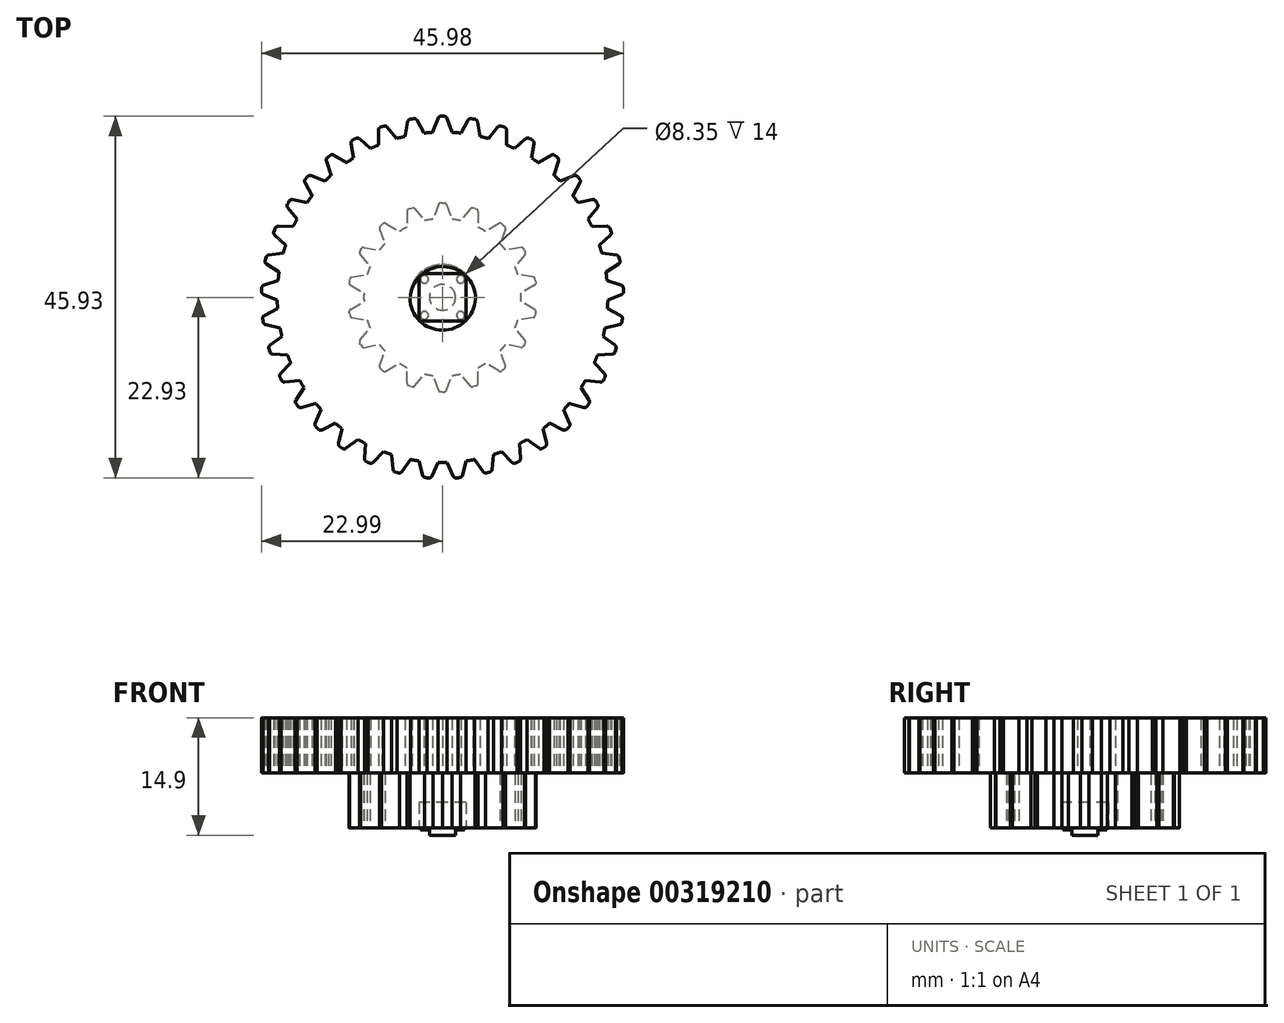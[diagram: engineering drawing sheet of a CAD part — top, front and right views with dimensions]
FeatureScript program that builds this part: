
annotation { "Feature Type Name" : "Feature", "Feature Type Description" : "" }
export const myFeature = defineFeature(function(context is Context, id is Id, definition is map)
    precondition{}
    {
        {
            var Q0;
            Q0=qCreatedBy(makeId("Top.planeOp"),FACE);
            var sketch = newSketch(context, id + "F0", { "sketchPlane" : qUnion([Q0])});
            skCircle(sketch, "E0", {"center": v(0, 0) * mm, "radius": 11 * mm, "construction": true});
            skCircle(sketch, "E1", {"center": v(0, 0) * mm, "radius": 10 * mm});
            skCircle(sketch, "E2", {"center": v(0, 0) * mm, "radius": 12 * mm, "construction": true});
            skPoint(sketch, "E3", {"position": v(10, 0) * mm});
            skPoint(sketch, "E4", {"position": v(11, 0) * mm});
            skPoint(sketch, "E5", {"position": v(12, 0) * mm});
            skLineSegment(sketch, "E6", {"start": v(-0.52, 11.8) * mm, "end": v(-1.2, 9.93) * mm});
            skLineSegment(sketch, "E7", {"start": v(0, 9.19) * mm, "end": v(0, 12) * mm});
            skLineSegment(sketch, "E8", {"start": v(0, 12) * mm, "end": v(-0.24, 12) * mm});
            skPoint(sketch, "E9.visualSharp", {"position": v(-0.45, 12) * mm});
            skArc(sketch, "E9.filletArc", {"start": v(-0.24, 12) * mm, "mid": v(-0.41, 11.94) * mm, "end": v(-0.52, 11.8) * mm});
            skLineSegment(sketch, "E10.MirrorCS", {"start": v(0, 12) * mm, "end": v(0.24, 12) * mm});
            skArc(sketch, "E11.MirrorCS", {"start": v(0.24, 12) * mm, "mid": v(0.41, 11.94) * mm, "end": v(0.52, 11.8) * mm});
            skLineSegment(sketch, "E12.MirrorCS", {"start": v(0.52, 11.8) * mm, "end": v(1.2, 9.93) * mm});
            skLineSegment(sketch, "E13.1.0", {"start": v(-3.55, 11.26) * mm, "end": v(-2.27, 9.74) * mm});
            skLineSegment(sketch, "E13.1.1", {"start": v(-4.52, 10.9) * mm, "end": v(-4.52, 8.92) * mm});
            skArc(sketch, "E13.1.2", {"start": v(-3.87, 11.36) * mm, "mid": v(-3.7, 11.36) * mm, "end": v(-3.55, 11.26) * mm});
            skArc(sketch, "E13.1.3", {"start": v(-4.33, 11.19) * mm, "mid": v(-4.47, 11.08) * mm, "end": v(-4.52, 10.9) * mm});
            skLineSegment(sketch, "E13.1.4", {"start": v(-4.1, 11.28) * mm, "end": v(-3.87, 11.36) * mm});
            skLineSegment(sketch, "E13.1.5", {"start": v(-4.1, 11.28) * mm, "end": v(-4.33, 11.19) * mm});
            skLineSegment(sketch, "E13.2.0", {"start": v(-7.19, 9.37) * mm, "end": v(-5.46, 8.38) * mm});
            skLineSegment(sketch, "E13.2.1", {"start": v(-7.98, 8.7) * mm, "end": v(-7.3, 6.83) * mm});
            skArc(sketch, "E13.2.2", {"start": v(-7.52, 9.35) * mm, "mid": v(-7.36, 9.41) * mm, "end": v(-7.19, 9.37) * mm});
            skArc(sketch, "E13.2.3", {"start": v(-7.9, 9.03) * mm, "mid": v(-8, 8.88) * mm, "end": v(-7.98, 8.7) * mm});
            skLineSegment(sketch, "E13.2.4", {"start": v(-7.71, 9.2) * mm, "end": v(-7.52, 9.35) * mm});
            skLineSegment(sketch, "E13.2.5", {"start": v(-7.71, 9.2) * mm, "end": v(-7.9, 9.03) * mm});
            skLineSegment(sketch, "E13.3.0", {"start": v(-9.96, 6.35) * mm, "end": v(-8, 6) * mm});
            skLineSegment(sketch, "E13.3.1", {"start": v(-10.48, 5.45) * mm, "end": v(-9.2, 3.92) * mm});
            skArc(sketch, "E13.3.2", {"start": v(-10.27, 6.2) * mm, "mid": v(-10.13, 6.33) * mm, "end": v(-9.96, 6.35) * mm});
            skArc(sketch, "E13.3.3", {"start": v(-10.51, 5.79) * mm, "mid": v(-10.55, 5.61) * mm, "end": v(-10.48, 5.45) * mm});
            skLineSegment(sketch, "E13.3.4", {"start": v(-10.4, 6) * mm, "end": v(-10.27, 6.2) * mm});
            skLineSegment(sketch, "E13.3.5", {"start": v(-10.4, 6) * mm, "end": v(-10.51, 5.79) * mm});
            skLineSegment(sketch, "E13.4.0", {"start": v(-11.53, 2.56) * mm, "end": v(-9.57, 2.9) * mm});
            skLineSegment(sketch, "E13.4.1", {"start": v(-11.7, 1.54) * mm, "end": v(-9.99, 0.54) * mm});
            skArc(sketch, "E13.4.2", {"start": v(-11.77, 2.32) * mm, "mid": v(-11.69, 2.48) * mm, "end": v(-11.53, 2.56) * mm});
            skArc(sketch, "E13.4.3", {"start": v(-11.86, 1.84) * mm, "mid": v(-11.83, 1.67) * mm, "end": v(-11.7, 1.54) * mm});
            skLineSegment(sketch, "E13.4.4", {"start": v(-11.82, 2.08) * mm, "end": v(-11.77, 2.32) * mm});
            skLineSegment(sketch, "E13.4.5", {"start": v(-11.82, 2.08) * mm, "end": v(-11.86, 1.84) * mm});
            skLineSegment(sketch, "E13.5.0", {"start": v(-11.7, -1.54) * mm, "end": v(-9.99, -0.54) * mm});
            skLineSegment(sketch, "E13.5.1", {"start": v(-11.53, -2.56) * mm, "end": v(-9.57, -2.9) * mm});
            skArc(sketch, "E13.5.2", {"start": v(-11.86, -1.84) * mm, "mid": v(-11.83, -1.67) * mm, "end": v(-11.7, -1.54) * mm});
            skArc(sketch, "E13.5.3", {"start": v(-11.77, -2.32) * mm, "mid": v(-11.69, -2.48) * mm, "end": v(-11.53, -2.56) * mm});
            skLineSegment(sketch, "E13.5.4", {"start": v(-11.82, -2.08) * mm, "end": v(-11.86, -1.84) * mm});
            skLineSegment(sketch, "E13.5.5", {"start": v(-11.82, -2.08) * mm, "end": v(-11.77, -2.32) * mm});
            skLineSegment(sketch, "E13.6.0", {"start": v(-10.48, -5.45) * mm, "end": v(-9.2, -3.92) * mm});
            skLineSegment(sketch, "E13.6.1", {"start": v(-9.96, -6.35) * mm, "end": v(-8, -6) * mm});
            skArc(sketch, "E13.6.2", {"start": v(-10.51, -5.79) * mm, "mid": v(-10.55, -5.61) * mm, "end": v(-10.48, -5.45) * mm});
            skArc(sketch, "E13.6.3", {"start": v(-10.27, -6.2) * mm, "mid": v(-10.13, -6.33) * mm, "end": v(-9.96, -6.35) * mm});
            skLineSegment(sketch, "E13.6.4", {"start": v(-10.4, -6) * mm, "end": v(-10.51, -5.79) * mm});
            skLineSegment(sketch, "E13.6.5", {"start": v(-10.4, -6) * mm, "end": v(-10.27, -6.2) * mm});
            skLineSegment(sketch, "E13.7.0", {"start": v(-7.98, -8.7) * mm, "end": v(-7.3, -6.83) * mm});
            skLineSegment(sketch, "E13.7.1", {"start": v(-7.19, -9.37) * mm, "end": v(-5.46, -8.38) * mm});
            skArc(sketch, "E13.7.2", {"start": v(-7.9, -9.03) * mm, "mid": v(-8, -8.88) * mm, "end": v(-7.98, -8.7) * mm});
            skArc(sketch, "E13.7.3", {"start": v(-7.52, -9.35) * mm, "mid": v(-7.36, -9.41) * mm, "end": v(-7.19, -9.37) * mm});
            skLineSegment(sketch, "E13.7.4", {"start": v(-7.71, -9.2) * mm, "end": v(-7.9, -9.03) * mm});
            skLineSegment(sketch, "E13.7.5", {"start": v(-7.71, -9.2) * mm, "end": v(-7.52, -9.35) * mm});
            skLineSegment(sketch, "E13.8.0", {"start": v(-4.52, -10.9) * mm, "end": v(-4.52, -8.92) * mm});
            skLineSegment(sketch, "E13.8.1", {"start": v(-3.55, -11.26) * mm, "end": v(-2.27, -9.74) * mm});
            skArc(sketch, "E13.8.2", {"start": v(-4.33, -11.19) * mm, "mid": v(-4.47, -11.08) * mm, "end": v(-4.52, -10.9) * mm});
            skArc(sketch, "E13.8.3", {"start": v(-3.87, -11.36) * mm, "mid": v(-3.7, -11.36) * mm, "end": v(-3.55, -11.26) * mm});
            skLineSegment(sketch, "E13.8.4", {"start": v(-4.1, -11.28) * mm, "end": v(-4.33, -11.19) * mm});
            skLineSegment(sketch, "E13.8.5", {"start": v(-4.1, -11.28) * mm, "end": v(-3.87, -11.36) * mm});
            skLineSegment(sketch, "E13.9.0", {"start": v(-0.52, -11.8) * mm, "end": v(-1.2, -9.93) * mm});
            skLineSegment(sketch, "E13.9.1", {"start": v(0.52, -11.8) * mm, "end": v(1.2, -9.93) * mm});
            skArc(sketch, "E13.9.2", {"start": v(-0.24, -12) * mm, "mid": v(-0.41, -11.94) * mm, "end": v(-0.52, -11.8) * mm});
            skArc(sketch, "E13.9.3", {"start": v(0.24, -12) * mm, "mid": v(0.41, -11.94) * mm, "end": v(0.52, -11.8) * mm});
            skLineSegment(sketch, "E13.9.4", {"start": v(0, -12) * mm, "end": v(-0.24, -12) * mm});
            skLineSegment(sketch, "E13.9.5", {"start": v(0, -12) * mm, "end": v(0.24, -12) * mm});
            skLineSegment(sketch, "E13.10.0", {"start": v(3.55, -11.26) * mm, "end": v(2.27, -9.74) * mm});
            skLineSegment(sketch, "E13.10.1", {"start": v(4.52, -10.9) * mm, "end": v(4.52, -8.92) * mm});
            skArc(sketch, "E13.10.2", {"start": v(3.87, -11.36) * mm, "mid": v(3.7, -11.36) * mm, "end": v(3.55, -11.26) * mm});
            skArc(sketch, "E13.10.3", {"start": v(4.33, -11.19) * mm, "mid": v(4.47, -11.08) * mm, "end": v(4.52, -10.9) * mm});
            skLineSegment(sketch, "E13.10.4", {"start": v(4.1, -11.28) * mm, "end": v(3.87, -11.36) * mm});
            skLineSegment(sketch, "E13.10.5", {"start": v(4.1, -11.28) * mm, "end": v(4.33, -11.19) * mm});
            skLineSegment(sketch, "E13.11.0", {"start": v(7.19, -9.37) * mm, "end": v(5.46, -8.38) * mm});
            skLineSegment(sketch, "E13.11.1", {"start": v(7.98, -8.7) * mm, "end": v(7.3, -6.83) * mm});
            skArc(sketch, "E13.11.2", {"start": v(7.52, -9.35) * mm, "mid": v(7.36, -9.41) * mm, "end": v(7.19, -9.37) * mm});
            skArc(sketch, "E13.11.3", {"start": v(7.9, -9.03) * mm, "mid": v(8, -8.88) * mm, "end": v(7.98, -8.7) * mm});
            skLineSegment(sketch, "E13.11.4", {"start": v(7.71, -9.2) * mm, "end": v(7.52, -9.35) * mm});
            skLineSegment(sketch, "E13.11.5", {"start": v(7.71, -9.2) * mm, "end": v(7.9, -9.03) * mm});
            skLineSegment(sketch, "E13.12.0", {"start": v(9.96, -6.35) * mm, "end": v(8, -6) * mm});
            skLineSegment(sketch, "E13.12.1", {"start": v(10.48, -5.45) * mm, "end": v(9.2, -3.92) * mm});
            skArc(sketch, "E13.12.2", {"start": v(10.27, -6.2) * mm, "mid": v(10.13, -6.33) * mm, "end": v(9.96, -6.35) * mm});
            skArc(sketch, "E13.12.3", {"start": v(10.51, -5.79) * mm, "mid": v(10.55, -5.61) * mm, "end": v(10.48, -5.45) * mm});
            skLineSegment(sketch, "E13.12.4", {"start": v(10.4, -6) * mm, "end": v(10.27, -6.2) * mm});
            skLineSegment(sketch, "E13.12.5", {"start": v(10.4, -6) * mm, "end": v(10.51, -5.79) * mm});
            skLineSegment(sketch, "E13.13.0", {"start": v(11.53, -2.56) * mm, "end": v(9.57, -2.9) * mm});
            skLineSegment(sketch, "E13.13.1", {"start": v(11.7, -1.54) * mm, "end": v(9.99, -0.54) * mm});
            skArc(sketch, "E13.13.2", {"start": v(11.77, -2.32) * mm, "mid": v(11.69, -2.48) * mm, "end": v(11.53, -2.56) * mm});
            skArc(sketch, "E13.13.3", {"start": v(11.86, -1.84) * mm, "mid": v(11.83, -1.67) * mm, "end": v(11.7, -1.54) * mm});
            skLineSegment(sketch, "E13.13.4", {"start": v(11.82, -2.08) * mm, "end": v(11.77, -2.32) * mm});
            skLineSegment(sketch, "E13.13.5", {"start": v(11.82, -2.08) * mm, "end": v(11.86, -1.84) * mm});
            skLineSegment(sketch, "E13.14.0", {"start": v(11.7, 1.54) * mm, "end": v(9.99, 0.54) * mm});
            skLineSegment(sketch, "E13.14.1", {"start": v(11.53, 2.56) * mm, "end": v(9.57, 2.9) * mm});
            skArc(sketch, "E13.14.2", {"start": v(11.86, 1.84) * mm, "mid": v(11.83, 1.67) * mm, "end": v(11.7, 1.54) * mm});
            skArc(sketch, "E13.14.3", {"start": v(11.77, 2.32) * mm, "mid": v(11.69, 2.48) * mm, "end": v(11.53, 2.56) * mm});
            skLineSegment(sketch, "E13.14.4", {"start": v(11.82, 2.08) * mm, "end": v(11.86, 1.84) * mm});
            skLineSegment(sketch, "E13.14.5", {"start": v(11.82, 2.08) * mm, "end": v(11.77, 2.32) * mm});
            skLineSegment(sketch, "E13.15.0", {"start": v(10.48, 5.45) * mm, "end": v(9.2, 3.92) * mm});
            skLineSegment(sketch, "E13.15.1", {"start": v(9.96, 6.35) * mm, "end": v(8, 6) * mm});
            skArc(sketch, "E13.15.2", {"start": v(10.51, 5.79) * mm, "mid": v(10.55, 5.61) * mm, "end": v(10.48, 5.45) * mm});
            skArc(sketch, "E13.15.3", {"start": v(10.27, 6.2) * mm, "mid": v(10.13, 6.33) * mm, "end": v(9.96, 6.35) * mm});
            skLineSegment(sketch, "E13.15.4", {"start": v(10.4, 6) * mm, "end": v(10.51, 5.79) * mm});
            skLineSegment(sketch, "E13.15.5", {"start": v(10.4, 6) * mm, "end": v(10.27, 6.2) * mm});
            skLineSegment(sketch, "E13.16.0", {"start": v(7.98, 8.7) * mm, "end": v(7.3, 6.83) * mm});
            skLineSegment(sketch, "E13.16.1", {"start": v(7.19, 9.37) * mm, "end": v(5.46, 8.38) * mm});
            skArc(sketch, "E13.16.2", {"start": v(7.9, 9.03) * mm, "mid": v(8, 8.88) * mm, "end": v(7.98, 8.7) * mm});
            skArc(sketch, "E13.16.3", {"start": v(7.52, 9.35) * mm, "mid": v(7.36, 9.41) * mm, "end": v(7.19, 9.37) * mm});
            skLineSegment(sketch, "E13.16.4", {"start": v(7.71, 9.2) * mm, "end": v(7.9, 9.03) * mm});
            skLineSegment(sketch, "E13.16.5", {"start": v(7.71, 9.2) * mm, "end": v(7.52, 9.35) * mm});
            skLineSegment(sketch, "E13.17.0", {"start": v(4.52, 10.9) * mm, "end": v(4.52, 8.92) * mm});
            skLineSegment(sketch, "E13.17.1", {"start": v(3.55, 11.26) * mm, "end": v(2.27, 9.74) * mm});
            skArc(sketch, "E13.17.2", {"start": v(4.33, 11.19) * mm, "mid": v(4.47, 11.08) * mm, "end": v(4.52, 10.9) * mm});
            skArc(sketch, "E13.17.3", {"start": v(3.87, 11.36) * mm, "mid": v(3.7, 11.36) * mm, "end": v(3.55, 11.26) * mm});
            skLineSegment(sketch, "E13.17.4", {"start": v(4.1, 11.28) * mm, "end": v(4.33, 11.19) * mm});
            skLineSegment(sketch, "E13.17.5", {"start": v(4.1, 11.28) * mm, "end": v(3.87, 11.36) * mm});
            skCircle(sketch, "E14", {"center": v(0, 0) * mm, "radius": 4.17 * mm});
            skSolve(sketch);
        }
        {
            var Q0;
            Q0 = qSketchRegion(id + "F0", true);
            extrude(context, id + "F1", {"entities" : qUnion([Q0]), "depth" : 7 * mm});
        }
        {
            var Q0;
            Q0=makeQuery(id+"F1.opExtrude","CAP_FACE",FACE,{"disambiguationData":[OSD([sQuery(id+"F0.wireOp",EDGE,"E1"),sQuery(id+"F0.wireOp",EDGE,"E6"),sQuery(id+"F0.wireOp",EDGE,"E8"),sQuery(id+"F0.wireOp",EDGE,"E9.filletArc"),sQuery(id+"F0.wireOp",EDGE,"E10.MirrorCS"),sQuery(id+"F0.wireOp",EDGE,"E11.MirrorCS"),sQuery(id+"F0.wireOp",EDGE,"E12.MirrorCS"),sQuery(id+"F0.wireOp",EDGE,"E13.1.0"),sQuery(id+"F0.wireOp",EDGE,"E13.1.1"),sQuery(id+"F0.wireOp",EDGE,"E13.1.2"),sQuery(id+"F0.wireOp",EDGE,"E13.1.3"),sQuery(id+"F0.wireOp",EDGE,"E13.1.4"),sQuery(id+"F0.wireOp",EDGE,"E13.1.5"),sQuery(id+"F0.wireOp",EDGE,"E13.2.0"),sQuery(id+"F0.wireOp",EDGE,"E13.2.1"),sQuery(id+"F0.wireOp",EDGE,"E13.2.2"),sQuery(id+"F0.wireOp",EDGE,"E13.2.3"),sQuery(id+"F0.wireOp",EDGE,"E13.2.4"),sQuery(id+"F0.wireOp",EDGE,"E13.2.5"),sQuery(id+"F0.wireOp",EDGE,"E13.3.0"),sQuery(id+"F0.wireOp",EDGE,"E13.3.1"),sQuery(id+"F0.wireOp",EDGE,"E13.3.2"),sQuery(id+"F0.wireOp",EDGE,"E13.3.3"),sQuery(id+"F0.wireOp",EDGE,"E13.3.4"),sQuery(id+"F0.wireOp",EDGE,"E13.3.5"),sQuery(id+"F0.wireOp",EDGE,"E13.4.0"),sQuery(id+"F0.wireOp",EDGE,"E13.4.1"),sQuery(id+"F0.wireOp",EDGE,"E13.4.2"),sQuery(id+"F0.wireOp",EDGE,"E13.4.3"),sQuery(id+"F0.wireOp",EDGE,"E13.4.4"),sQuery(id+"F0.wireOp",EDGE,"E13.4.5"),sQuery(id+"F0.wireOp",EDGE,"E13.5.0"),sQuery(id+"F0.wireOp",EDGE,"E13.5.1"),sQuery(id+"F0.wireOp",EDGE,"E13.5.2"),sQuery(id+"F0.wireOp",EDGE,"E13.5.3"),sQuery(id+"F0.wireOp",EDGE,"E13.5.4"),sQuery(id+"F0.wireOp",EDGE,"E13.5.5"),sQuery(id+"F0.wireOp",EDGE,"E13.6.0"),sQuery(id+"F0.wireOp",EDGE,"E13.6.1"),sQuery(id+"F0.wireOp",EDGE,"E13.6.2"),sQuery(id+"F0.wireOp",EDGE,"E13.6.3"),sQuery(id+"F0.wireOp",EDGE,"E13.6.4"),sQuery(id+"F0.wireOp",EDGE,"E13.6.5"),sQuery(id+"F0.wireOp",EDGE,"E13.7.0"),sQuery(id+"F0.wireOp",EDGE,"E13.7.1"),sQuery(id+"F0.wireOp",EDGE,"E13.7.2"),sQuery(id+"F0.wireOp",EDGE,"E13.7.3"),sQuery(id+"F0.wireOp",EDGE,"E13.7.4"),sQuery(id+"F0.wireOp",EDGE,"E13.7.5"),sQuery(id+"F0.wireOp",EDGE,"E13.8.0"),sQuery(id+"F0.wireOp",EDGE,"E13.8.1"),sQuery(id+"F0.wireOp",EDGE,"E13.8.2"),sQuery(id+"F0.wireOp",EDGE,"E13.8.3"),sQuery(id+"F0.wireOp",EDGE,"E13.8.4"),sQuery(id+"F0.wireOp",EDGE,"E13.8.5"),sQuery(id+"F0.wireOp",EDGE,"E13.9.0"),sQuery(id+"F0.wireOp",EDGE,"E13.9.1"),sQuery(id+"F0.wireOp",EDGE,"E13.9.2"),sQuery(id+"F0.wireOp",EDGE,"E13.9.3"),sQuery(id+"F0.wireOp",EDGE,"E13.9.4"),sQuery(id+"F0.wireOp",EDGE,"E13.9.5"),sQuery(id+"F0.wireOp",EDGE,"E13.10.0"),sQuery(id+"F0.wireOp",EDGE,"E13.10.1"),sQuery(id+"F0.wireOp",EDGE,"E13.10.2"),sQuery(id+"F0.wireOp",EDGE,"E13.10.3"),sQuery(id+"F0.wireOp",EDGE,"E13.10.4"),sQuery(id+"F0.wireOp",EDGE,"E13.10.5"),sQuery(id+"F0.wireOp",EDGE,"E13.11.0"),sQuery(id+"F0.wireOp",EDGE,"E13.11.1"),sQuery(id+"F0.wireOp",EDGE,"E13.11.2"),sQuery(id+"F0.wireOp",EDGE,"E13.11.3"),sQuery(id+"F0.wireOp",EDGE,"E13.11.4"),sQuery(id+"F0.wireOp",EDGE,"E13.11.5"),sQuery(id+"F0.wireOp",EDGE,"E13.12.0"),sQuery(id+"F0.wireOp",EDGE,"E13.12.1"),sQuery(id+"F0.wireOp",EDGE,"E13.12.2"),sQuery(id+"F0.wireOp",EDGE,"E13.12.3"),sQuery(id+"F0.wireOp",EDGE,"E13.12.4"),sQuery(id+"F0.wireOp",EDGE,"E13.12.5"),sQuery(id+"F0.wireOp",EDGE,"E13.13.0"),sQuery(id+"F0.wireOp",EDGE,"E13.13.1"),sQuery(id+"F0.wireOp",EDGE,"E13.13.2"),sQuery(id+"F0.wireOp",EDGE,"E13.13.3"),sQuery(id+"F0.wireOp",EDGE,"E13.13.4"),sQuery(id+"F0.wireOp",EDGE,"E13.13.5"),sQuery(id+"F0.wireOp",EDGE,"E13.14.0"),sQuery(id+"F0.wireOp",EDGE,"E13.14.1"),sQuery(id+"F0.wireOp",EDGE,"E13.14.2"),sQuery(id+"F0.wireOp",EDGE,"E13.14.3"),sQuery(id+"F0.wireOp",EDGE,"E13.14.4"),sQuery(id+"F0.wireOp",EDGE,"E13.14.5"),sQuery(id+"F0.wireOp",EDGE,"E13.15.0"),sQuery(id+"F0.wireOp",EDGE,"E13.15.1"),sQuery(id+"F0.wireOp",EDGE,"E13.15.2"),sQuery(id+"F0.wireOp",EDGE,"E13.15.3"),sQuery(id+"F0.wireOp",EDGE,"E13.15.4"),sQuery(id+"F0.wireOp",EDGE,"E13.15.5"),sQuery(id+"F0.wireOp",EDGE,"E13.16.0"),sQuery(id+"F0.wireOp",EDGE,"E13.16.1"),sQuery(id+"F0.wireOp",EDGE,"E13.16.2"),sQuery(id+"F0.wireOp",EDGE,"E13.16.3"),sQuery(id+"F0.wireOp",EDGE,"E13.16.4"),sQuery(id+"F0.wireOp",EDGE,"E13.16.5"),sQuery(id+"F0.wireOp",EDGE,"E13.17.0"),sQuery(id+"F0.wireOp",EDGE,"E13.17.1"),sQuery(id+"F0.wireOp",EDGE,"E13.17.2"),sQuery(id+"F0.wireOp",EDGE,"E13.17.3"),sQuery(id+"F0.wireOp",EDGE,"E13.17.4"),sQuery(id+"F0.wireOp",EDGE,"E13.17.5"),sQuery(id+"F0.wireOp",EDGE,"E14")])],"isStart":false});
            var sketch = newSketch(context, id + "F2", { "sketchPlane" : qUnion([Q0])});
            skCircle(sketch, "E15.0", {"center": v(0, 0) * mm, "radius": 4.17 * mm});
            skCircle(sketch, "E16", {"center": v(0, 0) * mm, "radius": 21 * mm});
            skCircle(sketch, "E17", {"center": v(0, 0) * mm, "radius": 22 * mm, "construction": true});
            skCircle(sketch, "E18", {"center": v(0, 0) * mm, "radius": 23 * mm, "construction": true});
            skLineSegment(sketch, "E19", {"start": v(-0.6, 22.73) * mm, "end": v(-1.24, 20.96) * mm});
            skLineSegment(sketch, "E20", {"start": v(0, 23) * mm, "end": v(-0.22, 23) * mm});
            skPoint(sketch, "E21.visualSharp", {"position": v(-0.5, 23) * mm});
            skArc(sketch, "E21.filletArc", {"start": v(-0.22, 23) * mm, "mid": v(-0.45, 22.92) * mm, "end": v(-0.6, 22.73) * mm});
            skArc(sketch, "E22.MirrorCS", {"start": v(0.22, 23) * mm, "mid": v(0.45, 22.92) * mm, "end": v(0.6, 22.73) * mm});
            skLineSegment(sketch, "E23.MirrorCS", {"start": v(0.6, 22.73) * mm, "end": v(1.24, 20.96) * mm});
            skLineSegment(sketch, "E24.MirrorCS", {"start": v(0, 23) * mm, "end": v(0.22, 23) * mm});
            skLineSegment(sketch, "E25.1.0", {"start": v(-4.43, 22.3) * mm, "end": v(-4.76, 20.45) * mm});
            skArc(sketch, "E25.1.1", {"start": v(-4.1, 22.63) * mm, "mid": v(-4.32, 22.52) * mm, "end": v(-4.43, 22.3) * mm});
            skLineSegment(sketch, "E25.1.2", {"start": v(-3.89, 22.67) * mm, "end": v(-4.1, 22.63) * mm});
            skLineSegment(sketch, "E25.1.3", {"start": v(-3.89, 22.67) * mm, "end": v(-3.67, 22.7) * mm});
            skArc(sketch, "E25.1.4", {"start": v(-3.67, 22.7) * mm, "mid": v(-3.43, 22.67) * mm, "end": v(-3.26, 22.5) * mm});
            skLineSegment(sketch, "E25.1.5", {"start": v(-3.26, 22.5) * mm, "end": v(-2.32, 20.87) * mm});
            skLineSegment(sketch, "E25.2.0", {"start": v(-8.13, 21.24) * mm, "end": v(-8.15, 19.35) * mm});
            skArc(sketch, "E25.2.1", {"start": v(-7.87, 21.6) * mm, "mid": v(-8.06, 21.46) * mm, "end": v(-8.13, 21.24) * mm});
            skLineSegment(sketch, "E25.2.2", {"start": v(-7.66, 21.69) * mm, "end": v(-7.87, 21.6) * mm});
            skLineSegment(sketch, "E25.2.3", {"start": v(-7.66, 21.69) * mm, "end": v(-7.45, 21.76) * mm});
            skArc(sketch, "E25.2.4", {"start": v(-7.45, 21.76) * mm, "mid": v(-7.21, 21.76) * mm, "end": v(-7.01, 21.63) * mm});
            skLineSegment(sketch, "E25.2.5", {"start": v(-7.01, 21.63) * mm, "end": v(-5.82, 20.18) * mm});
            skLineSegment(sketch, "E25.3.0", {"start": v(-11.6, 19.56) * mm, "end": v(-11.3, 17.7) * mm});
            skArc(sketch, "E25.3.1", {"start": v(-11.41, 19.97) * mm, "mid": v(-11.57, 19.8) * mm, "end": v(-11.6, 19.56) * mm});
            skLineSegment(sketch, "E25.3.2", {"start": v(-11.22, 20.08) * mm, "end": v(-11.41, 19.97) * mm});
            skLineSegment(sketch, "E25.3.3", {"start": v(-11.22, 20.08) * mm, "end": v(-11.02, 20.19) * mm});
            skArc(sketch, "E25.3.4", {"start": v(-11.02, 20.19) * mm, "mid": v(-10.79, 20.23) * mm, "end": v(-10.57, 20.14) * mm});
            skLineSegment(sketch, "E25.3.5", {"start": v(-10.57, 20.14) * mm, "end": v(-9.14, 18.9) * mm});
            skLineSegment(sketch, "E25.4.0", {"start": v(-14.74, 17.31) * mm, "end": v(-14.13, 15.53) * mm});
            skArc(sketch, "E25.4.1", {"start": v(-14.62, 17.75) * mm, "mid": v(-14.75, 17.55) * mm, "end": v(-14.74, 17.31) * mm});
            skLineSegment(sketch, "E25.4.2", {"start": v(-14.45, 17.9) * mm, "end": v(-14.62, 17.75) * mm});
            skLineSegment(sketch, "E25.4.3", {"start": v(-14.45, 17.9) * mm, "end": v(-14.27, 18.03) * mm});
            skArc(sketch, "E25.4.4", {"start": v(-14.27, 18.03) * mm, "mid": v(-14.05, 18.12) * mm, "end": v(-13.82, 18.06) * mm});
            skLineSegment(sketch, "E25.4.5", {"start": v(-13.82, 18.06) * mm, "end": v(-12.2, 17.09) * mm});
            skLineSegment(sketch, "E25.5.0", {"start": v(-17.46, 14.57) * mm, "end": v(-16.56, 12.92) * mm});
            skArc(sketch, "E25.5.1", {"start": v(-17.41, 15.03) * mm, "mid": v(-17.5, 14.8) * mm, "end": v(-17.46, 14.57) * mm});
            skLineSegment(sketch, "E25.5.2", {"start": v(-17.27, 15.2) * mm, "end": v(-17.41, 15.03) * mm});
            skLineSegment(sketch, "E25.5.3", {"start": v(-17.27, 15.2) * mm, "end": v(-17.12, 15.36) * mm});
            skArc(sketch, "E25.5.4", {"start": v(-17.12, 15.36) * mm, "mid": v(-16.91, 15.48) * mm, "end": v(-16.67, 15.47) * mm});
            skLineSegment(sketch, "E25.5.5", {"start": v(-16.67, 15.47) * mm, "end": v(-14.92, 14.78) * mm});
            skLineSegment(sketch, "E25.6.0", {"start": v(-19.67, 11.41) * mm, "end": v(-18.5, 9.94) * mm});
            skArc(sketch, "E25.6.1", {"start": v(-19.7, 11.87) * mm, "mid": v(-19.76, 11.64) * mm, "end": v(-19.67, 11.41) * mm});
            skLineSegment(sketch, "E25.6.2", {"start": v(-19.59, 12.06) * mm, "end": v(-19.7, 11.87) * mm});
            skLineSegment(sketch, "E25.6.3", {"start": v(-19.59, 12.06) * mm, "end": v(-19.47, 12.25) * mm});
            skArc(sketch, "E25.6.4", {"start": v(-19.47, 12.25) * mm, "mid": v(-19.28, 12.4) * mm, "end": v(-19.05, 12.43) * mm});
            skLineSegment(sketch, "E25.6.5", {"start": v(-19.05, 12.43) * mm, "end": v(-17.2, 12.05) * mm});
            skLineSegment(sketch, "E25.7.0", {"start": v(-21.32, 7.92) * mm, "end": v(-19.91, 6.67) * mm});
            skArc(sketch, "E25.7.1", {"start": v(-21.42, 8.37) * mm, "mid": v(-21.44, 8.13) * mm, "end": v(-21.32, 7.92) * mm});
            skLineSegment(sketch, "E25.7.2", {"start": v(-21.34, 8.58) * mm, "end": v(-21.42, 8.37) * mm});
            skLineSegment(sketch, "E25.7.3", {"start": v(-21.34, 8.58) * mm, "end": v(-21.26, 8.78) * mm});
            skArc(sketch, "E25.7.4", {"start": v(-21.26, 8.78) * mm, "mid": v(-21.1, 8.96) * mm, "end": v(-20.87, 9.03) * mm});
            skLineSegment(sketch, "E25.7.5", {"start": v(-20.87, 9.03) * mm, "end": v(-18.99, 8.97) * mm});
            skLineSegment(sketch, "E25.8.0", {"start": v(-22.35, 4.2) * mm, "end": v(-20.75, 3.2) * mm});
            skArc(sketch, "E25.8.1", {"start": v(-22.53, 4.63) * mm, "mid": v(-22.5, 4.39) * mm, "end": v(-22.35, 4.2) * mm});
            skLineSegment(sketch, "E25.8.2", {"start": v(-22.48, 4.85) * mm, "end": v(-22.53, 4.63) * mm});
            skLineSegment(sketch, "E25.8.3", {"start": v(-22.48, 4.85) * mm, "end": v(-22.43, 5.06) * mm});
            skArc(sketch, "E25.8.4", {"start": v(-22.43, 5.06) * mm, "mid": v(-22.31, 5.27) * mm, "end": v(-22.1, 5.37) * mm});
            skLineSegment(sketch, "E25.8.5", {"start": v(-22.1, 5.37) * mm, "end": v(-20.23, 5.63) * mm});
            skLineSegment(sketch, "E25.9.0", {"start": v(-22.74, 0.37) * mm, "end": v(-21, -0.35) * mm});
            skArc(sketch, "E25.9.1", {"start": v(-22.99, 0.75) * mm, "mid": v(-22.92, 0.52) * mm, "end": v(-22.74, 0.37) * mm});
            skLineSegment(sketch, "E25.9.2", {"start": v(-22.98, 0.98) * mm, "end": v(-22.99, 0.75) * mm});
            skLineSegment(sketch, "E25.9.3", {"start": v(-22.98, 0.98) * mm, "end": v(-22.97, 1.2) * mm});
            skArc(sketch, "E25.9.4", {"start": v(-22.97, 1.2) * mm, "mid": v(-22.88, 1.42) * mm, "end": v(-22.69, 1.56) * mm});
            skLineSegment(sketch, "E25.9.5", {"start": v(-22.69, 1.56) * mm, "end": v(-20.9, 2.13) * mm});
            skLineSegment(sketch, "E25.10.0", {"start": v(-22.47, -3.48) * mm, "end": v(-20.64, -3.9) * mm});
            skArc(sketch, "E25.10.1", {"start": v(-22.78, -3.14) * mm, "mid": v(-22.68, -3.36) * mm, "end": v(-22.47, -3.48) * mm});
            skLineSegment(sketch, "E25.10.2", {"start": v(-22.81, -2.92) * mm, "end": v(-22.78, -3.14) * mm});
            skLineSegment(sketch, "E25.10.3", {"start": v(-22.81, -2.92) * mm, "end": v(-22.84, -2.7) * mm});
            skArc(sketch, "E25.10.4", {"start": v(-22.84, -2.7) * mm, "mid": v(-22.8, -2.47) * mm, "end": v(-22.63, -2.3) * mm});
            skLineSegment(sketch, "E25.10.5", {"start": v(-22.63, -2.3) * mm, "end": v(-20.95, -1.43) * mm});
            skLineSegment(sketch, "E25.11.0", {"start": v(-21.56, -7.23) * mm, "end": v(-19.68, -7.32) * mm});
            skArc(sketch, "E25.11.1", {"start": v(-21.92, -6.95) * mm, "mid": v(-21.79, -7.14) * mm, "end": v(-21.56, -7.23) * mm});
            skLineSegment(sketch, "E25.11.2", {"start": v(-22, -6.73) * mm, "end": v(-21.92, -6.95) * mm});
            skLineSegment(sketch, "E25.11.3", {"start": v(-22, -6.73) * mm, "end": v(-22.05, -6.52) * mm});
            skArc(sketch, "E25.11.4", {"start": v(-22.05, -6.52) * mm, "mid": v(-22.05, -6.28) * mm, "end": v(-21.91, -6.09) * mm});
            skLineSegment(sketch, "E25.11.5", {"start": v(-21.91, -6.09) * mm, "end": v(-20.4, -4.95) * mm});
            skLineSegment(sketch, "E25.12.0", {"start": v(-20.03, -10.77) * mm, "end": v(-18.16, -10.54) * mm});
            skArc(sketch, "E25.12.1", {"start": v(-20.43, -10.55) * mm, "mid": v(-20.27, -10.72) * mm, "end": v(-20.03, -10.77) * mm});
            skLineSegment(sketch, "E25.12.2", {"start": v(-20.54, -10.35) * mm, "end": v(-20.43, -10.55) * mm});
            skLineSegment(sketch, "E25.12.3", {"start": v(-20.54, -10.35) * mm, "end": v(-20.64, -10.15) * mm});
            skArc(sketch, "E25.12.4", {"start": v(-20.64, -10.15) * mm, "mid": v(-20.67, -9.92) * mm, "end": v(-20.57, -9.7) * mm});
            skLineSegment(sketch, "E25.12.5", {"start": v(-20.57, -9.7) * mm, "end": v(-19.28, -8.33) * mm});
            skLineSegment(sketch, "E25.13.0", {"start": v(-17.92, -14) * mm, "end": v(-16.12, -13.46) * mm});
            skArc(sketch, "E25.13.1", {"start": v(-18.36, -13.85) * mm, "mid": v(-18.16, -14) * mm, "end": v(-17.92, -14) * mm});
            skLineSegment(sketch, "E25.13.2", {"start": v(-18.5, -13.68) * mm, "end": v(-18.36, -13.85) * mm});
            skLineSegment(sketch, "E25.13.3", {"start": v(-18.5, -13.68) * mm, "end": v(-18.62, -13.5) * mm});
            skArc(sketch, "E25.13.4", {"start": v(-18.62, -13.5) * mm, "mid": v(-18.7, -13.27) * mm, "end": v(-18.63, -13.04) * mm});
            skLineSegment(sketch, "E25.13.5", {"start": v(-18.63, -13.04) * mm, "end": v(-17.6, -11.47) * mm});
            skLineSegment(sketch, "E25.14.0", {"start": v(-15.3, -16.82) * mm, "end": v(-13.61, -16) * mm});
            skArc(sketch, "E25.14.1", {"start": v(-15.75, -16.76) * mm, "mid": v(-15.54, -16.86) * mm, "end": v(-15.3, -16.82) * mm});
            skLineSegment(sketch, "E25.14.2", {"start": v(-15.91, -16.6) * mm, "end": v(-15.75, -16.76) * mm});
            skLineSegment(sketch, "E25.14.3", {"start": v(-15.91, -16.6) * mm, "end": v(-16.07, -16.45) * mm});
            skArc(sketch, "E25.14.4", {"start": v(-16.07, -16.45) * mm, "mid": v(-16.19, -16.24) * mm, "end": v(-16.16, -16) * mm});
            skLineSegment(sketch, "E25.14.5", {"start": v(-16.16, -16) * mm, "end": v(-15.4, -14.28) * mm});
            skLineSegment(sketch, "E25.15.0", {"start": v(-12.24, -19.17) * mm, "end": v(-10.71, -18.06) * mm});
            skArc(sketch, "E25.15.1", {"start": v(-12.7, -19.18) * mm, "mid": v(-12.46, -19.24) * mm, "end": v(-12.24, -19.17) * mm});
            skLineSegment(sketch, "E25.15.2", {"start": v(-12.88, -19.06) * mm, "end": v(-12.7, -19.18) * mm});
            skLineSegment(sketch, "E25.15.3", {"start": v(-12.88, -19.06) * mm, "end": v(-13.06, -18.93) * mm});
            skArc(sketch, "E25.15.4", {"start": v(-13.06, -18.93) * mm, "mid": v(-13.2, -18.74) * mm, "end": v(-13.22, -18.5) * mm});
            skLineSegment(sketch, "E25.15.5", {"start": v(-13.22, -18.5) * mm, "end": v(-12.77, -16.67) * mm});
            skLineSegment(sketch, "E25.16.0", {"start": v(-8.82, -20.96) * mm, "end": v(-7.5, -19.61) * mm});
            skArc(sketch, "E25.16.1", {"start": v(-9.27, -21.05) * mm, "mid": v(-9.03, -21.07) * mm, "end": v(-8.82, -20.96) * mm});
            skLineSegment(sketch, "E25.16.2", {"start": v(-9.47, -20.96) * mm, "end": v(-9.27, -21.05) * mm});
            skLineSegment(sketch, "E25.16.3", {"start": v(-9.47, -20.96) * mm, "end": v(-9.68, -20.86) * mm});
            skArc(sketch, "E25.16.4", {"start": v(-9.68, -20.86) * mm, "mid": v(-9.85, -20.7) * mm, "end": v(-9.9, -20.47) * mm});
            skLineSegment(sketch, "E25.16.5", {"start": v(-9.9, -20.47) * mm, "end": v(-9.76, -18.6) * mm});
            skLineSegment(sketch, "E25.17.0", {"start": v(-5.15, -22.15) * mm, "end": v(-4.08, -20.6) * mm});
            skArc(sketch, "E25.17.1", {"start": v(-5.58, -22.31) * mm, "mid": v(-5.34, -22.3) * mm, "end": v(-5.15, -22.15) * mm});
            skLineSegment(sketch, "E25.17.2", {"start": v(-5.8, -22.26) * mm, "end": v(-5.58, -22.31) * mm});
            skLineSegment(sketch, "E25.17.3", {"start": v(-5.8, -22.26) * mm, "end": v(-6.01, -22.2) * mm});
            skArc(sketch, "E25.17.4", {"start": v(-6.01, -22.2) * mm, "mid": v(-6.21, -22.07) * mm, "end": v(-6.3, -21.85) * mm});
            skLineSegment(sketch, "E25.17.5", {"start": v(-6.3, -21.85) * mm, "end": v(-6.48, -19.97) * mm});
            skLineSegment(sketch, "E25.18.0", {"start": v(-1.34, -22.7) * mm, "end": v(-0.54, -21) * mm});
            skArc(sketch, "E25.18.1", {"start": v(-1.73, -22.93) * mm, "mid": v(-1.5, -22.88) * mm, "end": v(-1.34, -22.7) * mm});
            skLineSegment(sketch, "E25.18.2", {"start": v(-1.95, -22.92) * mm, "end": v(-1.73, -22.93) * mm});
            skLineSegment(sketch, "E25.18.3", {"start": v(-1.95, -22.92) * mm, "end": v(-2.17, -22.9) * mm});
            skArc(sketch, "E25.18.4", {"start": v(-2.17, -22.9) * mm, "mid": v(-2.4, -22.8) * mm, "end": v(-2.52, -22.6) * mm});
            skLineSegment(sketch, "E25.18.5", {"start": v(-2.52, -22.6) * mm, "end": v(-3.01, -20.78) * mm});
            skLineSegment(sketch, "E25.19.0", {"start": v(2.52, -22.6) * mm, "end": v(3.01, -20.78) * mm});
            skArc(sketch, "E25.19.1", {"start": v(2.17, -22.9) * mm, "mid": v(2.4, -22.8) * mm, "end": v(2.52, -22.6) * mm});
            skLineSegment(sketch, "E25.19.2", {"start": v(1.95, -22.92) * mm, "end": v(2.17, -22.9) * mm});
            skLineSegment(sketch, "E25.19.3", {"start": v(1.95, -22.92) * mm, "end": v(1.73, -22.93) * mm});
            skArc(sketch, "E25.19.4", {"start": v(1.73, -22.93) * mm, "mid": v(1.5, -22.88) * mm, "end": v(1.34, -22.7) * mm});
            skLineSegment(sketch, "E25.19.5", {"start": v(1.34, -22.7) * mm, "end": v(0.54, -21) * mm});
            skLineSegment(sketch, "E25.20.0", {"start": v(6.3, -21.85) * mm, "end": v(6.48, -19.97) * mm});
            skArc(sketch, "E25.20.1", {"start": v(6.01, -22.2) * mm, "mid": v(6.21, -22.07) * mm, "end": v(6.3, -21.85) * mm});
            skLineSegment(sketch, "E25.20.2", {"start": v(5.8, -22.26) * mm, "end": v(6.01, -22.2) * mm});
            skLineSegment(sketch, "E25.20.3", {"start": v(5.8, -22.26) * mm, "end": v(5.58, -22.31) * mm});
            skArc(sketch, "E25.20.4", {"start": v(5.58, -22.31) * mm, "mid": v(5.34, -22.3) * mm, "end": v(5.15, -22.15) * mm});
            skLineSegment(sketch, "E25.20.5", {"start": v(5.15, -22.15) * mm, "end": v(4.08, -20.6) * mm});
            skLineSegment(sketch, "E25.21.0", {"start": v(9.9, -20.47) * mm, "end": v(9.76, -18.6) * mm});
            skArc(sketch, "E25.21.1", {"start": v(9.68, -20.86) * mm, "mid": v(9.85, -20.7) * mm, "end": v(9.9, -20.47) * mm});
            skLineSegment(sketch, "E25.21.2", {"start": v(9.47, -20.96) * mm, "end": v(9.68, -20.86) * mm});
            skLineSegment(sketch, "E25.21.3", {"start": v(9.47, -20.96) * mm, "end": v(9.27, -21.05) * mm});
            skArc(sketch, "E25.21.4", {"start": v(9.27, -21.05) * mm, "mid": v(9.03, -21.07) * mm, "end": v(8.82, -20.96) * mm});
            skLineSegment(sketch, "E25.21.5", {"start": v(8.82, -20.96) * mm, "end": v(7.5, -19.61) * mm});
            skLineSegment(sketch, "E25.22.0", {"start": v(13.22, -18.5) * mm, "end": v(12.77, -16.67) * mm});
            skArc(sketch, "E25.22.1", {"start": v(13.06, -18.93) * mm, "mid": v(13.2, -18.74) * mm, "end": v(13.22, -18.5) * mm});
            skLineSegment(sketch, "E25.22.2", {"start": v(12.88, -19.06) * mm, "end": v(13.06, -18.93) * mm});
            skLineSegment(sketch, "E25.22.3", {"start": v(12.88, -19.06) * mm, "end": v(12.7, -19.18) * mm});
            skArc(sketch, "E25.22.4", {"start": v(12.7, -19.18) * mm, "mid": v(12.46, -19.24) * mm, "end": v(12.24, -19.17) * mm});
            skLineSegment(sketch, "E25.22.5", {"start": v(12.24, -19.17) * mm, "end": v(10.71, -18.06) * mm});
            skLineSegment(sketch, "E25.23.0", {"start": v(16.16, -16) * mm, "end": v(15.4, -14.28) * mm});
            skArc(sketch, "E25.23.1", {"start": v(16.07, -16.45) * mm, "mid": v(16.19, -16.24) * mm, "end": v(16.16, -16) * mm});
            skLineSegment(sketch, "E25.23.2", {"start": v(15.91, -16.6) * mm, "end": v(16.07, -16.45) * mm});
            skLineSegment(sketch, "E25.23.3", {"start": v(15.91, -16.6) * mm, "end": v(15.75, -16.76) * mm});
            skArc(sketch, "E25.23.4", {"start": v(15.75, -16.76) * mm, "mid": v(15.54, -16.86) * mm, "end": v(15.3, -16.82) * mm});
            skLineSegment(sketch, "E25.23.5", {"start": v(15.3, -16.82) * mm, "end": v(13.61, -16) * mm});
            skLineSegment(sketch, "E25.24.0", {"start": v(18.63, -13.04) * mm, "end": v(17.6, -11.47) * mm});
            skArc(sketch, "E25.24.1", {"start": v(18.62, -13.5) * mm, "mid": v(18.7, -13.27) * mm, "end": v(18.63, -13.04) * mm});
            skLineSegment(sketch, "E25.24.2", {"start": v(18.5, -13.68) * mm, "end": v(18.62, -13.5) * mm});
            skLineSegment(sketch, "E25.24.3", {"start": v(18.5, -13.68) * mm, "end": v(18.36, -13.85) * mm});
            skArc(sketch, "E25.24.4", {"start": v(18.36, -13.85) * mm, "mid": v(18.16, -14) * mm, "end": v(17.92, -14) * mm});
            skLineSegment(sketch, "E25.24.5", {"start": v(17.92, -14) * mm, "end": v(16.12, -13.46) * mm});
            skLineSegment(sketch, "E25.25.0", {"start": v(20.57, -9.7) * mm, "end": v(19.28, -8.33) * mm});
            skArc(sketch, "E25.25.1", {"start": v(20.64, -10.15) * mm, "mid": v(20.67, -9.92) * mm, "end": v(20.57, -9.7) * mm});
            skLineSegment(sketch, "E25.25.2", {"start": v(20.54, -10.35) * mm, "end": v(20.64, -10.15) * mm});
            skLineSegment(sketch, "E25.25.3", {"start": v(20.54, -10.35) * mm, "end": v(20.43, -10.55) * mm});
            skArc(sketch, "E25.25.4", {"start": v(20.43, -10.55) * mm, "mid": v(20.27, -10.72) * mm, "end": v(20.03, -10.77) * mm});
            skLineSegment(sketch, "E25.25.5", {"start": v(20.03, -10.77) * mm, "end": v(18.16, -10.54) * mm});
            skLineSegment(sketch, "E25.26.0", {"start": v(21.91, -6.09) * mm, "end": v(20.4, -4.95) * mm});
            skArc(sketch, "E25.26.1", {"start": v(22.05, -6.52) * mm, "mid": v(22.05, -6.28) * mm, "end": v(21.91, -6.09) * mm});
            skLineSegment(sketch, "E25.26.2", {"start": v(22, -6.73) * mm, "end": v(22.05, -6.52) * mm});
            skLineSegment(sketch, "E25.26.3", {"start": v(22, -6.73) * mm, "end": v(21.92, -6.95) * mm});
            skArc(sketch, "E25.26.4", {"start": v(21.92, -6.95) * mm, "mid": v(21.79, -7.14) * mm, "end": v(21.56, -7.23) * mm});
            skLineSegment(sketch, "E25.26.5", {"start": v(21.56, -7.23) * mm, "end": v(19.68, -7.32) * mm});
            skLineSegment(sketch, "E25.27.0", {"start": v(22.63, -2.3) * mm, "end": v(20.95, -1.43) * mm});
            skArc(sketch, "E25.27.1", {"start": v(22.84, -2.7) * mm, "mid": v(22.8, -2.47) * mm, "end": v(22.63, -2.3) * mm});
            skLineSegment(sketch, "E25.27.2", {"start": v(22.81, -2.92) * mm, "end": v(22.84, -2.7) * mm});
            skLineSegment(sketch, "E25.27.3", {"start": v(22.81, -2.92) * mm, "end": v(22.78, -3.14) * mm});
            skArc(sketch, "E25.27.4", {"start": v(22.78, -3.14) * mm, "mid": v(22.68, -3.36) * mm, "end": v(22.47, -3.48) * mm});
            skLineSegment(sketch, "E25.27.5", {"start": v(22.47, -3.48) * mm, "end": v(20.64, -3.9) * mm});
            skLineSegment(sketch, "E25.28.0", {"start": v(22.69, 1.56) * mm, "end": v(20.9, 2.13) * mm});
            skArc(sketch, "E25.28.1", {"start": v(22.97, 1.2) * mm, "mid": v(22.88, 1.42) * mm, "end": v(22.69, 1.56) * mm});
            skLineSegment(sketch, "E25.28.2", {"start": v(22.98, 0.98) * mm, "end": v(22.97, 1.2) * mm});
            skLineSegment(sketch, "E25.28.3", {"start": v(22.98, 0.98) * mm, "end": v(22.99, 0.75) * mm});
            skArc(sketch, "E25.28.4", {"start": v(22.99, 0.75) * mm, "mid": v(22.92, 0.52) * mm, "end": v(22.74, 0.37) * mm});
            skLineSegment(sketch, "E25.28.5", {"start": v(22.74, 0.37) * mm, "end": v(21, -0.35) * mm});
            skLineSegment(sketch, "E25.29.0", {"start": v(22.1, 5.37) * mm, "end": v(20.23, 5.63) * mm});
            skArc(sketch, "E25.29.1", {"start": v(22.43, 5.06) * mm, "mid": v(22.31, 5.27) * mm, "end": v(22.1, 5.37) * mm});
            skLineSegment(sketch, "E25.29.2", {"start": v(22.48, 4.85) * mm, "end": v(22.43, 5.06) * mm});
            skLineSegment(sketch, "E25.29.3", {"start": v(22.48, 4.85) * mm, "end": v(22.53, 4.63) * mm});
            skArc(sketch, "E25.29.4", {"start": v(22.53, 4.63) * mm, "mid": v(22.5, 4.39) * mm, "end": v(22.35, 4.2) * mm});
            skLineSegment(sketch, "E25.29.5", {"start": v(22.35, 4.2) * mm, "end": v(20.75, 3.2) * mm});
            skLineSegment(sketch, "E25.30.0", {"start": v(20.87, 9.03) * mm, "end": v(18.99, 8.97) * mm});
            skArc(sketch, "E25.30.1", {"start": v(21.26, 8.78) * mm, "mid": v(21.1, 8.96) * mm, "end": v(20.87, 9.03) * mm});
            skLineSegment(sketch, "E25.30.2", {"start": v(21.34, 8.58) * mm, "end": v(21.26, 8.78) * mm});
            skLineSegment(sketch, "E25.30.3", {"start": v(21.34, 8.58) * mm, "end": v(21.42, 8.37) * mm});
            skArc(sketch, "E25.30.4", {"start": v(21.42, 8.37) * mm, "mid": v(21.44, 8.13) * mm, "end": v(21.32, 7.92) * mm});
            skLineSegment(sketch, "E25.30.5", {"start": v(21.32, 7.92) * mm, "end": v(19.91, 6.67) * mm});
            skLineSegment(sketch, "E25.31.0", {"start": v(19.05, 12.43) * mm, "end": v(17.2, 12.05) * mm});
            skArc(sketch, "E25.31.1", {"start": v(19.47, 12.25) * mm, "mid": v(19.28, 12.4) * mm, "end": v(19.05, 12.43) * mm});
            skLineSegment(sketch, "E25.31.2", {"start": v(19.59, 12.06) * mm, "end": v(19.47, 12.25) * mm});
            skLineSegment(sketch, "E25.31.3", {"start": v(19.59, 12.06) * mm, "end": v(19.7, 11.87) * mm});
            skArc(sketch, "E25.31.4", {"start": v(19.7, 11.87) * mm, "mid": v(19.76, 11.64) * mm, "end": v(19.67, 11.41) * mm});
            skLineSegment(sketch, "E25.31.5", {"start": v(19.67, 11.41) * mm, "end": v(18.5, 9.94) * mm});
            skLineSegment(sketch, "E25.32.0", {"start": v(16.67, 15.47) * mm, "end": v(14.92, 14.78) * mm});
            skArc(sketch, "E25.32.1", {"start": v(17.12, 15.36) * mm, "mid": v(16.91, 15.48) * mm, "end": v(16.67, 15.47) * mm});
            skLineSegment(sketch, "E25.32.2", {"start": v(17.27, 15.2) * mm, "end": v(17.12, 15.36) * mm});
            skLineSegment(sketch, "E25.32.3", {"start": v(17.27, 15.2) * mm, "end": v(17.41, 15.03) * mm});
            skArc(sketch, "E25.32.4", {"start": v(17.41, 15.03) * mm, "mid": v(17.5, 14.8) * mm, "end": v(17.46, 14.57) * mm});
            skLineSegment(sketch, "E25.32.5", {"start": v(17.46, 14.57) * mm, "end": v(16.56, 12.92) * mm});
            skLineSegment(sketch, "E25.33.0", {"start": v(13.82, 18.06) * mm, "end": v(12.2, 17.09) * mm});
            skArc(sketch, "E25.33.1", {"start": v(14.27, 18.03) * mm, "mid": v(14.05, 18.12) * mm, "end": v(13.82, 18.06) * mm});
            skLineSegment(sketch, "E25.33.2", {"start": v(14.45, 17.9) * mm, "end": v(14.27, 18.03) * mm});
            skLineSegment(sketch, "E25.33.3", {"start": v(14.45, 17.9) * mm, "end": v(14.62, 17.75) * mm});
            skArc(sketch, "E25.33.4", {"start": v(14.62, 17.75) * mm, "mid": v(14.75, 17.55) * mm, "end": v(14.74, 17.31) * mm});
            skLineSegment(sketch, "E25.33.5", {"start": v(14.74, 17.31) * mm, "end": v(14.13, 15.53) * mm});
            skLineSegment(sketch, "E25.34.0", {"start": v(10.57, 20.14) * mm, "end": v(9.14, 18.9) * mm});
            skArc(sketch, "E25.34.1", {"start": v(11.02, 20.19) * mm, "mid": v(10.79, 20.23) * mm, "end": v(10.57, 20.14) * mm});
            skLineSegment(sketch, "E25.34.2", {"start": v(11.22, 20.08) * mm, "end": v(11.02, 20.19) * mm});
            skLineSegment(sketch, "E25.34.3", {"start": v(11.22, 20.08) * mm, "end": v(11.41, 19.97) * mm});
            skArc(sketch, "E25.34.4", {"start": v(11.41, 19.97) * mm, "mid": v(11.57, 19.8) * mm, "end": v(11.6, 19.56) * mm});
            skLineSegment(sketch, "E25.34.5", {"start": v(11.6, 19.56) * mm, "end": v(11.3, 17.7) * mm});
            skLineSegment(sketch, "E25.35.0", {"start": v(7.01, 21.63) * mm, "end": v(5.82, 20.18) * mm});
            skArc(sketch, "E25.35.1", {"start": v(7.45, 21.76) * mm, "mid": v(7.21, 21.76) * mm, "end": v(7.01, 21.63) * mm});
            skLineSegment(sketch, "E25.35.2", {"start": v(7.66, 21.69) * mm, "end": v(7.45, 21.76) * mm});
            skLineSegment(sketch, "E25.35.3", {"start": v(7.66, 21.69) * mm, "end": v(7.87, 21.6) * mm});
            skArc(sketch, "E25.35.4", {"start": v(7.87, 21.6) * mm, "mid": v(8.06, 21.46) * mm, "end": v(8.13, 21.24) * mm});
            skLineSegment(sketch, "E25.35.5", {"start": v(8.13, 21.24) * mm, "end": v(8.15, 19.35) * mm});
            skLineSegment(sketch, "E25.36.0", {"start": v(3.26, 22.5) * mm, "end": v(2.32, 20.87) * mm});
            skArc(sketch, "E25.36.1", {"start": v(3.67, 22.7) * mm, "mid": v(3.43, 22.67) * mm, "end": v(3.26, 22.5) * mm});
            skLineSegment(sketch, "E25.36.2", {"start": v(3.89, 22.67) * mm, "end": v(3.67, 22.7) * mm});
            skLineSegment(sketch, "E25.36.3", {"start": v(3.89, 22.67) * mm, "end": v(4.1, 22.63) * mm});
            skArc(sketch, "E25.36.4", {"start": v(4.1, 22.63) * mm, "mid": v(4.32, 22.52) * mm, "end": v(4.43, 22.3) * mm});
            skLineSegment(sketch, "E25.36.5", {"start": v(4.43, 22.3) * mm, "end": v(4.76, 20.45) * mm});
            skSolve(sketch);
        }
        {
            var Q0;
            Q0=makeQuery(id+"F2.imprint","IMPRINT",FACE,{"disambiguationData":[TD([[makeQuery(id+"F2.imprint","IMPRINT",EDGE,{"derivedFrom":sQuery(id+"F2.wireOp",EDGE,"E15.0")}),-1.0]])]});
            var sketch = newSketch(context, id + "F3", { "sketchPlane" : qUnion([Q0])});
            skCircle(sketch, "E26", {"center": v(0.05, -0.28) * mm, "radius": 11 * mm, "construction": true});
            skCircle(sketch, "E27", {"center": v(0.05, -0.28) * mm, "radius": 10 * mm});
            skCircle(sketch, "E28", {"center": v(0.05, -0.28) * mm, "radius": 12 * mm, "construction": true});
            skPoint(sketch, "E29", {"position": v(10.05, -0.28) * mm});
            skPoint(sketch, "E30", {"position": v(11.05, -0.28) * mm});
            skPoint(sketch, "E31", {"position": v(12.05, -0.28) * mm});
            skLineSegment(sketch, "E32", {"start": v(-0.47, 11.52) * mm, "end": v(-1.15, 9.65) * mm});
            skLineSegment(sketch, "E33", {"start": v(0.05, 8.91) * mm, "end": v(0.05, 11.72) * mm});
            skLineSegment(sketch, "E34", {"start": v(0.05, 11.72) * mm, "end": v(-0.2, 11.72) * mm});
            skPoint(sketch, "E35.visualSharp", {"position": v(-0.4, 11.72) * mm});
            skArc(sketch, "E35.filletArc", {"start": v(-0.2, 11.72) * mm, "mid": v(-0.36, 11.66) * mm, "end": v(-0.47, 11.52) * mm});
            skLineSegment(sketch, "E36.MirrorCS", {"start": v(0.05, 11.72) * mm, "end": v(0.3, 11.72) * mm});
            skArc(sketch, "E37.MirrorCS", {"start": v(0.3, 11.72) * mm, "mid": v(0.47, 11.66) * mm, "end": v(0.57, 11.52) * mm});
            skLineSegment(sketch, "E38.MirrorCS", {"start": v(0.57, 11.52) * mm, "end": v(1.25, 9.65) * mm});
            skLineSegment(sketch, "E39.1.0", {"start": v(-3.5, 10.99) * mm, "end": v(-2.21, 9.46) * mm});
            skLineSegment(sketch, "E39.1.1", {"start": v(-4.47, 10.63) * mm, "end": v(-4.47, 8.64) * mm});
            skArc(sketch, "E39.1.2", {"start": v(-3.82, 11.08) * mm, "mid": v(-3.64, 11.09) * mm, "end": v(-3.5, 10.99) * mm});
            skArc(sketch, "E39.1.3", {"start": v(-4.28, 10.91) * mm, "mid": v(-4.42, 10.8) * mm, "end": v(-4.47, 10.63) * mm});
            skLineSegment(sketch, "E39.1.4", {"start": v(-4.05, 11) * mm, "end": v(-3.82, 11.08) * mm});
            skLineSegment(sketch, "E39.1.5", {"start": v(-4.05, 11) * mm, "end": v(-4.28, 10.91) * mm});
            skLineSegment(sketch, "E39.2.0", {"start": v(-7.13, 9.1) * mm, "end": v(-5.4, 8.1) * mm});
            skLineSegment(sketch, "E39.2.1", {"start": v(-7.93, 8.43) * mm, "end": v(-7.25, 6.56) * mm});
            skArc(sketch, "E39.2.2", {"start": v(-7.47, 9.07) * mm, "mid": v(-7.3, 9.14) * mm, "end": v(-7.13, 9.1) * mm});
            skArc(sketch, "E39.2.3", {"start": v(-7.85, 8.76) * mm, "mid": v(-7.94, 8.6) * mm, "end": v(-7.93, 8.43) * mm});
            skLineSegment(sketch, "E39.2.4", {"start": v(-7.66, 8.92) * mm, "end": v(-7.47, 9.07) * mm});
            skLineSegment(sketch, "E39.2.5", {"start": v(-7.66, 8.92) * mm, "end": v(-7.85, 8.76) * mm});
            skLineSegment(sketch, "E39.3.0", {"start": v(-9.9, 6.07) * mm, "end": v(-7.94, 5.73) * mm});
            skLineSegment(sketch, "E39.3.1", {"start": v(-10.43, 5.17) * mm, "end": v(-9.15, 3.65) * mm});
            skArc(sketch, "E39.3.2", {"start": v(-10.21, 5.93) * mm, "mid": v(-10.08, 6.05) * mm, "end": v(-9.9, 6.07) * mm});
            skArc(sketch, "E39.3.3", {"start": v(-10.46, 5.51) * mm, "mid": v(-10.5, 5.34) * mm, "end": v(-10.43, 5.17) * mm});
            skLineSegment(sketch, "E39.3.4", {"start": v(-10.34, 5.72) * mm, "end": v(-10.21, 5.93) * mm});
            skLineSegment(sketch, "E39.3.5", {"start": v(-10.34, 5.72) * mm, "end": v(-10.46, 5.51) * mm});
            skLineSegment(sketch, "E39.4.0", {"start": v(-11.48, 2.29) * mm, "end": v(-9.52, 2.63) * mm});
            skLineSegment(sketch, "E39.4.1", {"start": v(-11.66, 1.26) * mm, "end": v(-9.93, 0.27) * mm});
            skArc(sketch, "E39.4.2", {"start": v(-11.72, 2.05) * mm, "mid": v(-11.63, 2.2) * mm, "end": v(-11.48, 2.29) * mm});
            skArc(sketch, "E39.4.3", {"start": v(-11.8, 1.57) * mm, "mid": v(-11.78, 1.4) * mm, "end": v(-11.66, 1.26) * mm});
            skLineSegment(sketch, "E39.4.4", {"start": v(-11.77, 1.8) * mm, "end": v(-11.72, 2.05) * mm});
            skLineSegment(sketch, "E39.4.5", {"start": v(-11.77, 1.8) * mm, "end": v(-11.8, 1.57) * mm});
            skLineSegment(sketch, "E39.5.0", {"start": v(-11.66, -1.81) * mm, "end": v(-9.93, -0.82) * mm});
            skLineSegment(sketch, "E39.5.1", {"start": v(-11.48, -2.84) * mm, "end": v(-9.52, -3.18) * mm});
            skArc(sketch, "E39.5.2", {"start": v(-11.8, -2.12) * mm, "mid": v(-11.78, -1.94) * mm, "end": v(-11.66, -1.81) * mm});
            skArc(sketch, "E39.5.3", {"start": v(-11.72, -2.6) * mm, "mid": v(-11.63, -2.76) * mm, "end": v(-11.48, -2.84) * mm});
            skLineSegment(sketch, "E39.5.4", {"start": v(-11.77, -2.36) * mm, "end": v(-11.8, -2.12) * mm});
            skLineSegment(sketch, "E39.5.5", {"start": v(-11.77, -2.36) * mm, "end": v(-11.72, -2.6) * mm});
            skLineSegment(sketch, "E39.6.0", {"start": v(-10.43, -5.72) * mm, "end": v(-9.15, -4.2) * mm});
            skLineSegment(sketch, "E39.6.1", {"start": v(-9.9, -6.63) * mm, "end": v(-7.94, -6.28) * mm});
            skArc(sketch, "E39.6.2", {"start": v(-10.46, -6.06) * mm, "mid": v(-10.5, -5.89) * mm, "end": v(-10.43, -5.72) * mm});
            skArc(sketch, "E39.6.3", {"start": v(-10.21, -6.48) * mm, "mid": v(-10.08, -6.6) * mm, "end": v(-9.9, -6.63) * mm});
            skLineSegment(sketch, "E39.6.4", {"start": v(-10.34, -6.28) * mm, "end": v(-10.46, -6.06) * mm});
            skLineSegment(sketch, "E39.6.5", {"start": v(-10.34, -6.28) * mm, "end": v(-10.21, -6.48) * mm});
            skLineSegment(sketch, "E39.7.0", {"start": v(-7.93, -8.98) * mm, "end": v(-7.25, -7.1) * mm});
            skLineSegment(sketch, "E39.7.1", {"start": v(-7.13, -9.65) * mm, "end": v(-5.4, -8.65) * mm});
            skArc(sketch, "E39.7.2", {"start": v(-7.85, -9.3) * mm, "mid": v(-7.94, -9.16) * mm, "end": v(-7.93, -8.98) * mm});
            skArc(sketch, "E39.7.3", {"start": v(-7.47, -9.62) * mm, "mid": v(-7.3, -9.69) * mm, "end": v(-7.13, -9.65) * mm});
            skLineSegment(sketch, "E39.7.4", {"start": v(-7.66, -9.47) * mm, "end": v(-7.85, -9.3) * mm});
            skLineSegment(sketch, "E39.7.5", {"start": v(-7.66, -9.47) * mm, "end": v(-7.47, -9.62) * mm});
            skLineSegment(sketch, "E39.8.0", {"start": v(-4.47, -11.18) * mm, "end": v(-4.47, -9.2) * mm});
            skLineSegment(sketch, "E39.8.1", {"start": v(-3.5, -11.54) * mm, "end": v(-2.21, -10.02) * mm});
            skArc(sketch, "E39.8.2", {"start": v(-4.28, -11.46) * mm, "mid": v(-4.42, -11.35) * mm, "end": v(-4.47, -11.18) * mm});
            skArc(sketch, "E39.8.3", {"start": v(-3.82, -11.63) * mm, "mid": v(-3.64, -11.64) * mm, "end": v(-3.5, -11.54) * mm});
            skLineSegment(sketch, "E39.8.4", {"start": v(-4.05, -11.55) * mm, "end": v(-4.28, -11.46) * mm});
            skLineSegment(sketch, "E39.8.5", {"start": v(-4.05, -11.55) * mm, "end": v(-3.82, -11.63) * mm});
            skLineSegment(sketch, "E39.9.0", {"start": v(-0.47, -12.07) * mm, "end": v(-1.15, -10.2) * mm});
            skLineSegment(sketch, "E39.9.1", {"start": v(0.57, -12.07) * mm, "end": v(1.25, -10.2) * mm});
            skArc(sketch, "E39.9.2", {"start": v(-0.2, -12.27) * mm, "mid": v(-0.36, -12.22) * mm, "end": v(-0.47, -12.07) * mm});
            skArc(sketch, "E39.9.3", {"start": v(0.3, -12.27) * mm, "mid": v(0.47, -12.22) * mm, "end": v(0.57, -12.07) * mm});
            skLineSegment(sketch, "E39.9.4", {"start": v(0.05, -12.28) * mm, "end": v(-0.2, -12.27) * mm});
            skLineSegment(sketch, "E39.9.5", {"start": v(0.05, -12.28) * mm, "end": v(0.3, -12.27) * mm});
            skLineSegment(sketch, "E39.10.0", {"start": v(3.6, -11.54) * mm, "end": v(2.32, -10.02) * mm});
            skLineSegment(sketch, "E39.10.1", {"start": v(4.58, -11.18) * mm, "end": v(4.58, -9.2) * mm});
            skArc(sketch, "E39.10.2", {"start": v(3.93, -11.63) * mm, "mid": v(3.75, -11.64) * mm, "end": v(3.6, -11.54) * mm});
            skArc(sketch, "E39.10.3", {"start": v(4.38, -11.46) * mm, "mid": v(4.52, -11.35) * mm, "end": v(4.58, -11.18) * mm});
            skLineSegment(sketch, "E39.10.4", {"start": v(4.16, -11.55) * mm, "end": v(3.93, -11.63) * mm});
            skLineSegment(sketch, "E39.10.5", {"start": v(4.16, -11.55) * mm, "end": v(4.38, -11.46) * mm});
            skLineSegment(sketch, "E39.11.0", {"start": v(7.24, -9.65) * mm, "end": v(5.51, -8.65) * mm});
            skLineSegment(sketch, "E39.11.1", {"start": v(8.03, -8.98) * mm, "end": v(7.35, -7.1) * mm});
            skArc(sketch, "E39.11.2", {"start": v(7.58, -9.62) * mm, "mid": v(7.41, -9.69) * mm, "end": v(7.24, -9.65) * mm});
            skArc(sketch, "E39.11.3", {"start": v(7.95, -9.3) * mm, "mid": v(8.04, -9.16) * mm, "end": v(8.03, -8.98) * mm});
            skLineSegment(sketch, "E39.11.4", {"start": v(7.77, -9.47) * mm, "end": v(7.58, -9.62) * mm});
            skLineSegment(sketch, "E39.11.5", {"start": v(7.77, -9.47) * mm, "end": v(7.95, -9.3) * mm});
            skLineSegment(sketch, "E39.12.0", {"start": v(10, -6.63) * mm, "end": v(8.05, -6.28) * mm});
            skLineSegment(sketch, "E39.12.1", {"start": v(10.53, -5.72) * mm, "end": v(9.25, -4.2) * mm});
            skArc(sketch, "E39.12.2", {"start": v(10.32, -6.48) * mm, "mid": v(10.19, -6.6) * mm, "end": v(10, -6.63) * mm});
            skArc(sketch, "E39.12.3", {"start": v(10.56, -6.06) * mm, "mid": v(10.6, -5.89) * mm, "end": v(10.53, -5.72) * mm});
            skLineSegment(sketch, "E39.12.4", {"start": v(10.44, -6.28) * mm, "end": v(10.32, -6.48) * mm});
            skLineSegment(sketch, "E39.12.5", {"start": v(10.44, -6.28) * mm, "end": v(10.56, -6.06) * mm});
            skLineSegment(sketch, "E39.13.0", {"start": v(11.58, -2.84) * mm, "end": v(9.62, -3.18) * mm});
            skLineSegment(sketch, "E39.13.1", {"start": v(11.76, -1.81) * mm, "end": v(10.04, -0.82) * mm});
            skArc(sketch, "E39.13.2", {"start": v(11.82, -2.6) * mm, "mid": v(11.74, -2.76) * mm, "end": v(11.58, -2.84) * mm});
            skArc(sketch, "E39.13.3", {"start": v(11.9, -2.12) * mm, "mid": v(11.88, -1.94) * mm, "end": v(11.76, -1.81) * mm});
            skLineSegment(sketch, "E39.13.4", {"start": v(11.87, -2.36) * mm, "end": v(11.82, -2.6) * mm});
            skLineSegment(sketch, "E39.13.5", {"start": v(11.87, -2.36) * mm, "end": v(11.9, -2.12) * mm});
            skLineSegment(sketch, "E39.14.0", {"start": v(11.76, 1.26) * mm, "end": v(10.04, 0.27) * mm});
            skLineSegment(sketch, "E39.14.1", {"start": v(11.58, 2.29) * mm, "end": v(9.62, 2.63) * mm});
            skArc(sketch, "E39.14.2", {"start": v(11.9, 1.57) * mm, "mid": v(11.88, 1.4) * mm, "end": v(11.76, 1.26) * mm});
            skArc(sketch, "E39.14.3", {"start": v(11.82, 2.05) * mm, "mid": v(11.74, 2.2) * mm, "end": v(11.58, 2.29) * mm});
            skLineSegment(sketch, "E39.14.4", {"start": v(11.87, 1.8) * mm, "end": v(11.9, 1.57) * mm});
            skLineSegment(sketch, "E39.14.5", {"start": v(11.87, 1.8) * mm, "end": v(11.82, 2.05) * mm});
            skLineSegment(sketch, "E39.15.0", {"start": v(10.53, 5.17) * mm, "end": v(9.25, 3.65) * mm});
            skLineSegment(sketch, "E39.15.1", {"start": v(10, 6.07) * mm, "end": v(8.05, 5.73) * mm});
            skArc(sketch, "E39.15.2", {"start": v(10.56, 5.51) * mm, "mid": v(10.6, 5.34) * mm, "end": v(10.53, 5.17) * mm});
            skArc(sketch, "E39.15.3", {"start": v(10.32, 5.93) * mm, "mid": v(10.19, 6.05) * mm, "end": v(10, 6.07) * mm});
            skLineSegment(sketch, "E39.15.4", {"start": v(10.44, 5.72) * mm, "end": v(10.56, 5.51) * mm});
            skLineSegment(sketch, "E39.15.5", {"start": v(10.44, 5.72) * mm, "end": v(10.32, 5.93) * mm});
            skLineSegment(sketch, "E39.16.0", {"start": v(8.03, 8.43) * mm, "end": v(7.35, 6.56) * mm});
            skLineSegment(sketch, "E39.16.1", {"start": v(7.24, 9.1) * mm, "end": v(5.51, 8.1) * mm});
            skArc(sketch, "E39.16.2", {"start": v(7.95, 8.76) * mm, "mid": v(8.04, 8.6) * mm, "end": v(8.03, 8.43) * mm});
            skArc(sketch, "E39.16.3", {"start": v(7.58, 9.07) * mm, "mid": v(7.41, 9.14) * mm, "end": v(7.24, 9.1) * mm});
            skLineSegment(sketch, "E39.16.4", {"start": v(7.77, 8.92) * mm, "end": v(7.95, 8.76) * mm});
            skLineSegment(sketch, "E39.16.5", {"start": v(7.77, 8.92) * mm, "end": v(7.58, 9.07) * mm});
            skLineSegment(sketch, "E39.17.0", {"start": v(4.58, 10.63) * mm, "end": v(4.58, 8.64) * mm});
            skLineSegment(sketch, "E39.17.1", {"start": v(3.6, 10.99) * mm, "end": v(2.32, 9.46) * mm});
            skArc(sketch, "E39.17.2", {"start": v(4.38, 10.91) * mm, "mid": v(4.52, 10.8) * mm, "end": v(4.58, 10.63) * mm});
            skArc(sketch, "E39.17.3", {"start": v(3.93, 11.08) * mm, "mid": v(3.75, 11.09) * mm, "end": v(3.6, 10.99) * mm});
            skLineSegment(sketch, "E39.17.4", {"start": v(4.16, 11) * mm, "end": v(4.38, 10.91) * mm});
            skLineSegment(sketch, "E39.17.5", {"start": v(4.16, 11) * mm, "end": v(3.93, 11.08) * mm});
            skCircle(sketch, "E40", {"center": v(0.05, -0.28) * mm, "radius": 4.17 * mm});
            skSolve(sketch);
        }
        {
            var Q0;
            Q0 = qSketchRegion(id + "F3", true);
            extrude(context, id + "F4", {"entities" : qUnion([Q0]), "depth" : 7 * mm});
        }
        {
            var Q0;
            Q0 = qSketchRegion(id + "F2", true);
            extrude(context, id + "F5", {"entities" : qUnion([Q0]), "operationType" : NewBodyOperationType.ADD, "depth" : 7 * mm});
        }
        {
            var Q0;
            Q0=qCreatedBy(makeId("Top.planeOp"),FACE);
            var sketch = newSketch(context, id + "F6", { "sketchPlane" : qUnion([Q0])});
            skLineSegment(sketch, "E41.bottom", {"start": v(3, 3) * mm, "end": v(-3, 3) * mm});
            skLineSegment(sketch, "E41.top", {"start": v(3, -3) * mm, "end": v(-3, -3) * mm});
            skLineSegment(sketch, "E41.left", {"start": v(3, 3) * mm, "end": v(3, -3) * mm});
            skLineSegment(sketch, "E41.right", {"start": v(-3, 3) * mm, "end": v(-3, -3) * mm});
            skPoint(sketch, "E41.middle", {"position": v(0, 0) * mm});
            skSolve(sketch);
        }
        {
            var Q0;
            Q0=makeQuery(id+"F6.imprint","IMPRINT",FACE,{"disambiguationData":[TD([[makeQuery(id+"F6.imprint","IMPRINT",EDGE,{"derivedFrom":sQuery(id+"F6.wireOp",EDGE,"E41.bottom")}),1.0]])]});
            extrude(context, id + "F7", {"entities" : qUnion([Q0]), "depth" : 3.3 * mm, "offsetDistance" : 25 * mm});
        }
        {
            var Q0;
            Q0=makeQuery(id+"F7.opExtrude","CAP_FACE",FACE,{"disambiguationData":[OSD([sQuery(id+"F6.wireOp",EDGE,"E41.bottom"),sQuery(id+"F6.wireOp",EDGE,"E41.top"),sQuery(id+"F6.wireOp",EDGE,"E41.left"),sQuery(id+"F6.wireOp",EDGE,"E41.right")])],"isStart":true});
            var sketch = newSketch(context, id + "F8", { "sketchPlane" : qUnion([Q0])});
            skCircle(sketch, "E42", {"center": v(0, 0) * mm, "radius": 1.65 * mm});
            skCircle(sketch, "E43", {"center": v(-2.3, 2.3) * mm, "radius": 0.5 * mm});
            skLineSegment(sketch, "E44", {"start": v(-3, 3) * mm, "end": v(3, -3) * mm, "construction": true});
            skLineSegment(sketch, "E45", {"start": v(3, 3) * mm, "end": v(-3, -3) * mm, "construction": true});
            skCircle(sketch, "E46", {"center": v(2.3, 2.3) * mm, "radius": 0.5 * mm});
            skCircle(sketch, "E47", {"center": v(2.3, -2.3) * mm, "radius": 0.5 * mm});
            skCircle(sketch, "E48", {"center": v(-2.3, -2.3) * mm, "radius": 0.5 * mm});
            skSolve(sketch);
        }
        {
            var Q0;
            Q0 = qSketchRegion(id + "F8", true);
            extrude(context, id + "F9", {"entities" : qUnion([Q0]), "operationType" : NewBodyOperationType.ADD, "depth" : .2 * mm, "offsetDistance" : 25 * mm});
        }
        {
            var Q0;
            Q0=makeQuery(id+"F9.opExtrude","CAP_FACE",FACE,{"disambiguationData":[OSD([sQuery(id+"F8.wireOp",EDGE,"E42")])],"isStart":false});
            var sketch = newSketch(context, id + "F10", { "sketchPlane" : qUnion([Q0])});
            skCircle(sketch, "E49", {"center": v(0, 0) * mm, "radius": 1.65 * mm});
            skSolve(sketch);
        }
        {
            var Q0;
            Q0 = qSketchRegion(id + "F10", true);
            extrude(context, id + "F11", {"entities" : qUnion([Q0]), "operationType" : NewBodyOperationType.ADD, "depth" : .7 * mm, "offsetDistance" : 25 * mm});
        }
    });
